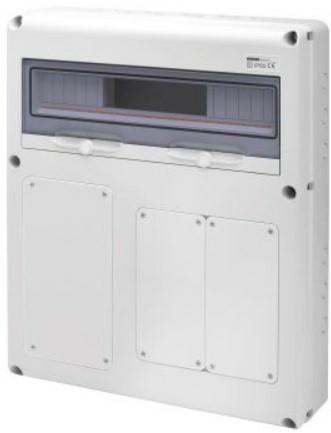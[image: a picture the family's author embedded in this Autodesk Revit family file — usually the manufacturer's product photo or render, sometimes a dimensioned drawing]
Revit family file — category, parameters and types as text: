
# Revit family: Building-QuadriIEC309-GEWISS-68QDIN-QUADRI-PRESE-20MOD_3PRESE_IB_VERT
name_source: partatom
category: Apparecchi elettrici
units: mm (PartAtom-declared; Revit-internal decimal feet)

## family parameters
Condiviso = No
Host = Superficie
Mantenere orientamento annotazione = Sì
Punto di calcolo locali = Sì
Quota connettore circolare = Usa diametro
Taglio con vuoti quando caricato = No
Tipo di parte = Normale

## types (1)
- GW68022N - Q-DIN 20M 1PR.BL.63A 2PR.BL.16/32A IP65
    Catalogo = BUILDING
    Catalogo Serie = 68 QDIN
    Classe isolamento = II
    Codice EAN = 8011564744899
    Codice Electrocod = 2242
    Colore = Grigio RAL 7035
    Conformità normativa = EN 60208 - EN 60670-1 - IEC 60670-24
    Descrizione = Q-DIN 20M 1PR.BL.63A 2PR.BL.16/32A IP65
    Glow Wire Test = 650°C
    Grado di protezione = IP65
    IDF = 6720abdd-bf8e-405e-981d-965ec1ef4bba
    IDT = c5faa6ce-0638-4a66-bbf1-3e08dc7c6100
    Immagine tipo = GW68022N.jpg
    L_Moduli = 380 mm  [stored 1.24672 ft]
    Modello = GW68022N
    N. coperchi ciechi in dotazione = 1 IB 16/32 A
    N. flange in dotazione = 1 IB 16/32 A
    N. mod. EN 50022 = 20
    N. prese IB alloggiabili: = 1 IB Vert. 63 A IP67 + 2 IB Vert. 16/32 A IP67
    N. prese alloggiabili = 1 IB Vert. 63 A IP67 + 2 IB Vert. 16/32 A IP67
    N_Moduli = 20 mm  [stored 0.0656168 ft]
    POMELLO = bianco
    PRESA = rosso
    Potenza dissipabile A (W) = 30
    Potenza dissipabile B (W) = 92
    Produttore = GEWISS S.p.A.
    Prospetto di default = 1219 mm
    Resistenza agli urti = IK08
    SEO = Quadretto
    STRUTTURA = RAL - 7035
    STRUTTURA ALTA = Poche
    Scheda Tecnica = https://www.gewiss.com
    Spostamento_S = 1000 mm  [stored 3.28084 ft]
    Temperatura di funzionamento = -25 ÷ +40 °C
    Temperatura di utilizzo = -25 +40 °C
    Termopressione con biglia = 70 °C
    Tipo versione = Vuoto
    Tipologia di installazione = Da parete
    URL = https://www.gewiss.com
    VETRO = Vetro
    Versione file RFA = 21.5

note: [stored X ft] marks values corroborated as IEEE doubles in the binary element streams (Revit-internal decimal feet)

## geometry (parser evidence)
native form markers: Sweep x5
no freeform markers — native parametric forms only
